# Revit family: Casement_41_H_Top_Hung_HD_Standard
name_source: partatom
category: Windows
revit_build: Autodesk Revit 2014 (Build: 20130308_1515(x64)
units: mm (PartAtom-declared; Revit-internal decimal feet)

## types (12) — shared parameters
Corrected Mullion Configuration = 2 mm  [stored 0.00656168 ft]
Custom Sash Height = 502 mm
Description = Window 41mm, Type H, Top hung, Heavy duty sash
Frame Profile Thickness = 41 mm  [stored 0.134514 ft]
Heavy Duty Sash = Yes
Limit Fixed Pane Height Max = 3000 mm  [stored 9.84252 ft]
Limit Fixed Pane Height Min = 200 mm  [stored 0.656168 ft]
Limit Fixed Pane Width Max = 3000 mm  [stored 9.84252 ft]
Limit Fixed Pane Width Min = 200 mm  [stored 0.656168 ft]
Limit Sash Height Max = 1200 mm  [stored 3.93701 ft]
Limit Sash Height Min = 300 mm  [stored 0.984252 ft]
Limit Sash Width Max = 1500 mm  [stored 4.92126 ft]
Limit Sash Width Min = 300 mm  [stored 0.984252 ft]
Limit Window Width Min = 388 mm
Manufacturer = Crealco
Max System DG Unit Thickness = 25 mm  [stored 0.082021 ft]
Model = Casement 41
Rough Width = 3 mm  [stored 0.00984252 ft]
Sash Side Gap = 44 mm
Standard Mullion Different = No
Standard Sash = No
URL = http://www.crealco.co.za
Wall Closure = By host
zero-valued in all types: Custom Frame Offset From Exterior

## per-type parameters (varying)
| type | Clearvue Insulated LowE SHGC Value | Clearvue Insulated LowE U Value | Clearvue Insulated SHGC Value | Clearvue Insulated U Value | Clearvue SHGC Value | Clearvue U Value | Custom Windload | Custom Window Height | Custom Window Width | Energy Advantage SHGC Value | Energy Advantage U Value | Intruderprufe Insulated LowE SHGC Value | Intruderprufe Insulated LowE U Value | Intruderprufe Insulated SHGC Value | Intruderprufe Insulated U Value | Intruderprufe LowE SHGC Value | Intruderprufe LowE U Value | Intruderprufe SHGC Value | Intruderprufe U Value | Toughened Safety SHGC Value | Toughened Safety U Value |
| 41-0615DT-HD-1000Pa | 0.688 | 3.76 | 0.688 | 3.84 | 0.437 | 6.18 | 1000 mm  [stored 3.28084 ft] | 1490 mm  [stored 4.88845 ft] | 590 mm  [stored 1.9357 ft] | 0.393 | 5.11 | 0.572 | 2.8 | 0.573 | 3.13 | 0.366 | 4.97 | 0.411 | 5.87 | 0.437 | 6.18 |
| 41-0615DT-HD-1500Pa | 0.688 | 3.76 | 0.688 | 3.84 | 0.437 | 6.18 | 1500 mm  [stored 4.92126 ft] | 1490 mm  [stored 4.88845 ft] | 590 mm  [stored 1.9357 ft] | 0.393 | 5.11 | 0.572 | 2.8 | 0.573 | 3.13 | 0.366 | 4.97 | 0.411 | 5.87 | 0.437 | 6.18 |
| 41-0615DT-HD-2000Pa | 0.688 | 3.76 | 0.688 | 3.84 | 0.437 | 6.18 | 2000 mm  [stored 6.56168 ft] | 1490 mm  [stored 4.88845 ft] | 590 mm  [stored 1.9357 ft] | 0.393 | 5.11 | 0.572 | 2.8 | 0.573 | 3.13 | 0.366 | 4.97 | 0.411 | 5.87 | 0.437 | 6.18 |
| 41-0915DT-HD-1000Pa | 0.688 | 4.05 | 0.688 | 4.13 | 0.497 | 6.14 | 1000 mm  [stored 3.28084 ft] | 1490 mm  [stored 4.88845 ft] | 890 mm  [stored 2.91995 ft] | 0.446 | 4.84 | 0.572 | 3 | 0.574 | 3.35 | 0.415 | 4.71 | 0.468 | 5.79 | 0.497 | 6.14 |
| 41-0915DT-HD-1500Pa | 0.688 | 4.05 | 0.688 | 4.13 | 0.497 | 6.14 | 1500 mm  [stored 4.92126 ft] | 1490 mm  [stored 4.88845 ft] | 890 mm  [stored 2.91995 ft] | 0.446 | 4.84 | 0.572 | 3 | 0.574 | 3.35 | 0.415 | 4.71 | 0.468 | 5.79 | 0.497 | 6.14 |
| 41-0915DT-HD-2000Pa | 0.688 | 4.05 | 0.688 | 4.13 | 0.497 | 6.14 | 2000 mm  [stored 6.56168 ft] | 1490 mm  [stored 4.88845 ft] | 890 mm  [stored 2.91995 ft] | 0.446 | 4.84 | 0.572 | 3 | 0.574 | 3.35 | 0.415 | 4.71 | 0.468 | 5.79 | 0.497 | 6.14 |
| 41-0618DT-HD-1000Pa | 0.715 | 3.91 | 0.715 | 3.97 | 0.479 | 6.15 | 1000 mm  [stored 3.28084 ft] | 1790 mm  [stored 5.8727 ft] | 590 mm  [stored 1.9357 ft] | 0.431 | 4.98 | 0.594 | 2.81 | 0.595 | 3.09 | 0.401 | 4.83 | 0.451 | 5.85 | 0.479 | 6.15 |
| 41-0618DT-HD-1500Pa | 0.715 | 3.91 | 0.715 | 3.97 | 0.479 | 6.15 | 1500 mm  [stored 4.92126 ft] | 1790 mm  [stored 5.8727 ft] | 590 mm  [stored 1.9357 ft] | 0.431 | 4.98 | 0.594 | 2.81 | 0.595 | 3.09 | 0.401 | 4.83 | 0.451 | 5.85 | 0.479 | 6.15 |
| 41-0618DT-HD-2000Pa | 0.715 | 3.91 | 0.715 | 3.97 | 0.479 | 6.15 | 2000 mm  [stored 6.56168 ft] | 1790 mm  [stored 5.8727 ft] | 590 mm  [stored 1.9357 ft] | 0.431 | 4.98 | 0.594 | 2.81 | 0.595 | 3.09 | 0.401 | 4.83 | 0.451 | 5.85 | 0.479 | 6.15 |
| 41-0918DT-HD-1000Pa | 0.715 | 4.22 | 0.715 | 4.29 | 0.539 | 6.11 | 1000 mm  [stored 3.28084 ft] | 1790 mm  [stored 5.8727 ft] | 890 mm  [stored 2.91995 ft] | 0.483 | 4.72 | 0.594 | 3.02 | 0.596 | 3.31 | 0.449 | 4.59 | 0.507 | 5.78 | 0.539 | 6.11 |
| 41-0918DT-HD-1500Pa | 0.715 | 4.22 | 0.715 | 4.29 | 0.539 | 6.11 | 1500 mm  [stored 4.92126 ft] | 1790 mm  [stored 5.8727 ft] | 890 mm  [stored 2.91995 ft] | 0.483 | 4.72 | 0.594 | 3.02 | 0.596 | 3.31 | 0.449 | 4.59 | 0.507 | 5.78 | 0.539 | 6.11 |
| 41-0918DT-HD-2000Pa | 0.715 | 4.22 | 0.715 | 4.29 | 0.539 | 6.11 | 2000 mm  [stored 6.56168 ft] | 1790 mm  [stored 5.8727 ft] | 890 mm  [stored 2.91995 ft] | 0.483 | 4.72 | 0.594 | 3.02 | 0.596 | 3.31 | 0.449 | 4.59 | 0.507 | 5.78 | 0.539 | 6.11 |

note: [stored X ft] marks values corroborated as IEEE doubles in the binary element streams (Revit-internal decimal feet)

## geometry (parser evidence)
native form markers: Sweep x20
no freeform markers — native parametric forms only
